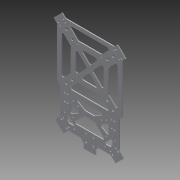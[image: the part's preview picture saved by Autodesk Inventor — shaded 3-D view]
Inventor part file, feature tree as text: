
AUTODESK INVENTOR PART (.ipt)
format: ipt  version: 2013 (Build 170138000, 138)  size: 12,763,648 bytes
history: native  units: mm
features: sketch x10, extrude x5, hole x5, other x2, fillet x2
ambient origin geometry x8: Origin, YZ Plane, XZ Plane, XY Plane, X Axis, Y Axis, Z Axis, Center Point
feature tree (24):
  other  "ソリッド1"
  extrude  "押し出し1"  Depth=115.0mm
  hole  "穴1"  [1 undecoded]
  hole  "穴2"  [1 undecoded]
  hole  "穴6"  [1 undecoded]
  hole  "穴7"  [1 undecoded]
  hole  "穴8"  [1 undecoded]
  extrude  "押し出し7"  TaperAngle=0.0deg  [1 undecoded]
  extrude  "押し出し8"  Depth=2.0mm TaperAngle=0.0deg
  extrude  "押し出し12"  Depth=3.2mm
  fillet  "フィレット1"  Radius=30.0mm
  extrude  "押し出し13"  Depth=8.0mm
  fillet  "フィレット2"  Radius=20.0mm
  sketch  "スケッチ1"
  sketch  "スケッチ2"
  sketch  "スケッチ3"
  sketch  "スケッチ9"
  sketch  "スケッチ11"
  sketch  "スケッチ12"
  sketch  "スケッチ13"
  sketch  "スケッチ14"
  sketch  "スケッチ17"
  sketch  "スケッチ19"
  other  "断面エッジを投影1"
note: 6 required parameter values undecoded (feature->parameter linkage not recoverable at this tier; creation-order binding heuristic only, values carry confidence <= 0.55)
